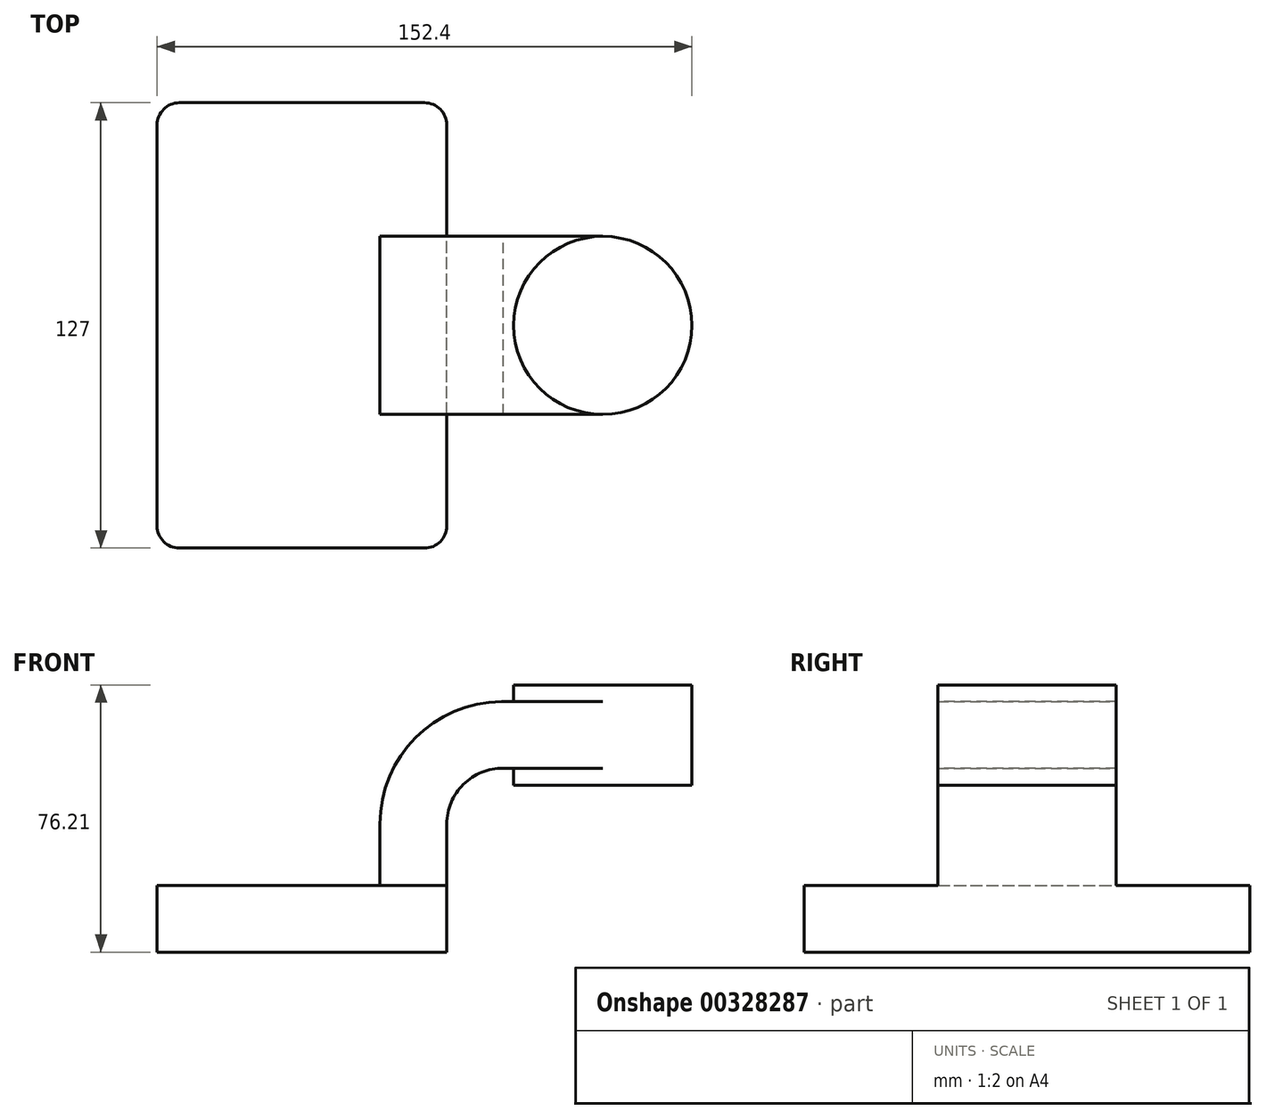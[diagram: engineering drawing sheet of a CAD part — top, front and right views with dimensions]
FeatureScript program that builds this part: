
annotation { "Feature Type Name" : "Feature", "Feature Type Description" : "" }
export const myFeature = defineFeature(function(context is Context, id is Id, definition is map)
    precondition{}
    {
        {
            var Q0;
            Q0=qCreatedBy(makeId("Front.planeOp"),FACE);
            var sketch = newSketch(context, id + "F0", { "sketchPlane" : qUnion([Q0])});
            skLineSegment(sketch, "E0.bottom", {"start": v(-41.27, -9.53) * mm, "end": v(41.27, -9.53) * mm});
            skLineSegment(sketch, "E0.top", {"start": v(-41.27, 9.53) * mm, "end": v(41.27, 9.53) * mm});
            skLineSegment(sketch, "E0.left", {"start": v(-41.27, -9.53) * mm, "end": v(-41.27, 9.52) * mm});
            skLineSegment(sketch, "E0.right", {"start": v(41.28, -9.53) * mm, "end": v(41.27, 9.52) * mm});
            skPoint(sketch, "E0.middle", {"position": v(0, 0) * mm});
            skLineSegment(sketch, "E1.bottom", {"start": v(60.33, 66.68) * mm, "end": v(111.13, 66.68) * mm});
            skLineSegment(sketch, "E1.top", {"start": v(60.33, 38.1) * mm, "end": v(111.13, 38.1) * mm});
            skLineSegment(sketch, "E1.left", {"start": v(60.33, 66.68) * mm, "end": v(60.33, 38.1) * mm});
            skLineSegment(sketch, "E1.right", {"start": v(111.13, 66.68) * mm, "end": v(111.13, 38.1) * mm});
            skPoint(sketch, "E1.middle", {"position": v(85.73, 52.39) * mm});
            skLineSegment(sketch, "E2", {"start": v(41.27, 9.52) * mm, "end": v(41.27, 27) * mm});
            skArc(sketch, "E3", {"start": v(41.28, 27) * mm, "mid": v(46, 38.3) * mm, "end": v(57.34, 42.88) * mm});
            skLineSegment(sketch, "E4", {"start": v(57.34, 42.88) * mm, "end": v(85.73, 42.88) * mm});
            skPoint(sketch, "E4.endSnap0", {"position": v(85.73, 38.1) * mm});
            skLineSegment(sketch, "E5.0", {"start": v(56.86, 61.93) * mm, "end": v(85.73, 61.93) * mm});
            skArc(sketch, "E5.1", {"start": v(22.23, 27) * mm, "mid": v(32.35, 51.6) * mm, "end": v(56.86, 61.93) * mm});
            skLineSegment(sketch, "E5.2", {"start": v(22.23, 9.52) * mm, "end": v(22.23, 27) * mm});
            skLineSegment(sketch, "E6", {"start": v(85.73, 38.1) * mm, "end": v(85.73, 66.68) * mm});
            skFitSpline(sketch, "E7", {"points": [v(-41.28, 9.53) * mm, v(56.86, 61.93) * mm], "startDerivative": vector(-1.66, 58.8) * mm, "endDerivative": vector(190.11, -1.31) * mm});
            skLineSegment(sketch, "E8", {"start": v(85.73, 66.68) * mm, "end": v(85.73, 38.1) * mm});
            skSolve(sketch);
        }
        {
            var Q0;
            Q0=makeQuery(id+"F0.imprint","IMPRINT",FACE,{"disambiguationData":[TD([[makeQuery(id+"F0.imprint","IMPRINT",EDGE,{"derivedFrom":sQuery(id+"F0.wireOp",EDGE,"E0.bottom")}),1.0]])]});
            extrude(context, id + "F1", {"entities" : qUnion([Q0]), "endBound" : BoundingType.SYMMETRIC, "depth" : 127 * mm});
        }
        {
            var Q0;
            {var subQ1=sQuery(id+"F0.wireOp",EDGE,"E2");Q0=makeQuery(id+"F0.imprint","IMPRINT",FACE,{"disambiguationData":[TD([[makeQuery(id+"F0.imprint","IMPRINT",EDGE,{"derivedFrom":subQ1}),1.0]])]});}
            var Q1;
            {var subQ0=sQuery(id+"F0.wireOp",EDGE,"E5.0");var subQ1=sQuery(id+"F0.wireOp",EDGE,"E1.left");var subQ2=makeQuery(id+"F0.imprint","INTERSECT",VERTEX,{"derivedFrom":[subQ1,subQ0]});Q1=makeQuery(id+"F0.imprint","IMPRINT",FACE,{"disambiguationData":[TD([[makeQuery(id+"F0.imprint","IMPRINT",EDGE,{"disambiguationData":[TD([[subQ2,-1.0]])],"derivedFrom":subQ1}),1.0]])]});}
            extrude(context, id + "F2", {"entities" : qUnion([Q0, Q1]), "operationType" : NewBodyOperationType.ADD, "endBound" : BoundingType.SYMMETRIC, "depth" : 50.8 * mm});
        }
        {
            var Q0;
            Q0=makeQuery(id+"F0.imprint","IMPRINT",FACE,{"disambiguationData":[TD([[makeQuery(id+"F0.imprint","IMPRINT",EDGE,{"derivedFrom":sQuery(id+"F0.wireOp",EDGE,"E5.1")}),1.0]])]});
            extrude(context, id + "F3", {"entities" : qUnion([Q0]), "operationType" : NewBodyOperationType.ADD, "endBound" : BoundingType.SYMMETRIC, "depth" : 15.88 * mm});
        }
        {
            var Q0;
            {var subQ4=sQuery(id+"F0.wireOp",EDGE,"E1.right");Q0=makeQuery(id+"F0.imprint","IMPRINT",FACE,{"disambiguationData":[TD([[makeQuery(id+"F0.imprint","IMPRINT",EDGE,{"derivedFrom":subQ4}),-1.0]])]});}
            var Q1;
            Q1=sQuery(id+"F0.wireOp",EDGE,"E8");
            revolve(context, id + "F4", {"operationType" : NewBodyOperationType.ADD, "entities" : qUnion([Q0]), "axis" : qUnion([Q1]), "revolveType" : RevolveType.FULL});
        }
        {
            var Q0;
            Q0=makeQuery(id+"F1.opExtrude","CAP_EDGE",EDGE,{"disambiguationData":[OSD([sQuery(id+"F0.wireOp",EDGE,"E0.left")])],"isStart":false});
            var Q1;
            Q1=makeQuery(id+"F1.opExtrude","CAP_EDGE",EDGE,{"disambiguationData":[OSD([sQuery(id+"F0.wireOp",EDGE,"E0.right")])],"isStart":false});
            var Q2;
            Q2=makeQuery(id+"F1.opExtrude","CAP_EDGE",EDGE,{"disambiguationData":[OSD([sQuery(id+"F0.wireOp",EDGE,"E0.left")])],"isStart":true});
            var Q3;
            Q3=makeQuery(id+"F1.opExtrude","CAP_EDGE",EDGE,{"disambiguationData":[OSD([sQuery(id+"F0.wireOp",EDGE,"E0.right")])],"isStart":true});
            fillet(context, id + "F5", {"entities" : qUnion([Q0, Q1, Q2, Q3]), "radius" : 6.35 * mm, "tangentPropagation" : true, "allowEdgeOverflow" : false});
        }
    });
